# Revit family: for update_74821XXX_NEW
name_source: partatom
category: Plumbing Fixtures
revit_build: Autodesk Revit 2018 (Build: 20170223_1515(x64)
units: mm (PartAtom-declared; Revit-internal decimal feet)

## family parameters
Always vertical = No
Cut with Voids When Loaded = No
OmniClass Number = 23.31.11.00
OmniClass Title = Faucets
Part Type = Normal
Room Calculation Point = No
Round Connector Dimension = Use Diameter
Shared = No
Work Plane-Based = Yes

## types (3) — shared parameters
Always visible = Yes
BIMobject category = Taps & Mixers
Connector Description = Water Inlet 9.5mm
Default Elevation = 1219.2 mm  [stored 4 ft]
Description = Zesis M33 Single lever kitchen mixer 150, metal pull-out spray, 2jet, sBox
Design country = Germany
Diameter = 10 mm
EAN code = 4059625464755
Edition number = 1
IFC Classification = Valve
Manufacturer = Hansgrohe
Manufacturer country = Germany
Manufacturer name = hansgrohe
Model = 74821XXX
OmniClass Code = 23-31 11 00
OmniClass Description = Faucets
Product Guid = 137b62ff-cbeb-48b3-a88a-780f20909cac
Product SKU = 74821XXX
Product data url = https://bimobject.com
Product family = Zesis M33
Product group = Kitchen mixers
Product name = Zesis M33 Single lever kitchen mixer 150, metal pull-out spray, 2jet, sBox
Product url = https://pro.hansgrohe.com
QR code = https://bimobject.com
URL = https://www.hansgrohe.com
Weight Net (Kg) = 3.2

## per-type parameters (varying)
| type | Material 1 |
| 670 Matte Black | Hansgrohe - Metal - 670 Matte Black |
| 800 Stainless Steel Optic | Hansgrohe - Metal - 800 Stainless Steel Optic |
| 000 Chrome | Hansgrohe - Metal - 000 Chrome |

note: [stored X ft] marks values corroborated as IEEE doubles in the binary element streams (Revit-internal decimal feet)

## geometry (parser evidence)
native form markers: Sweep x2
no freeform markers — native parametric forms only
